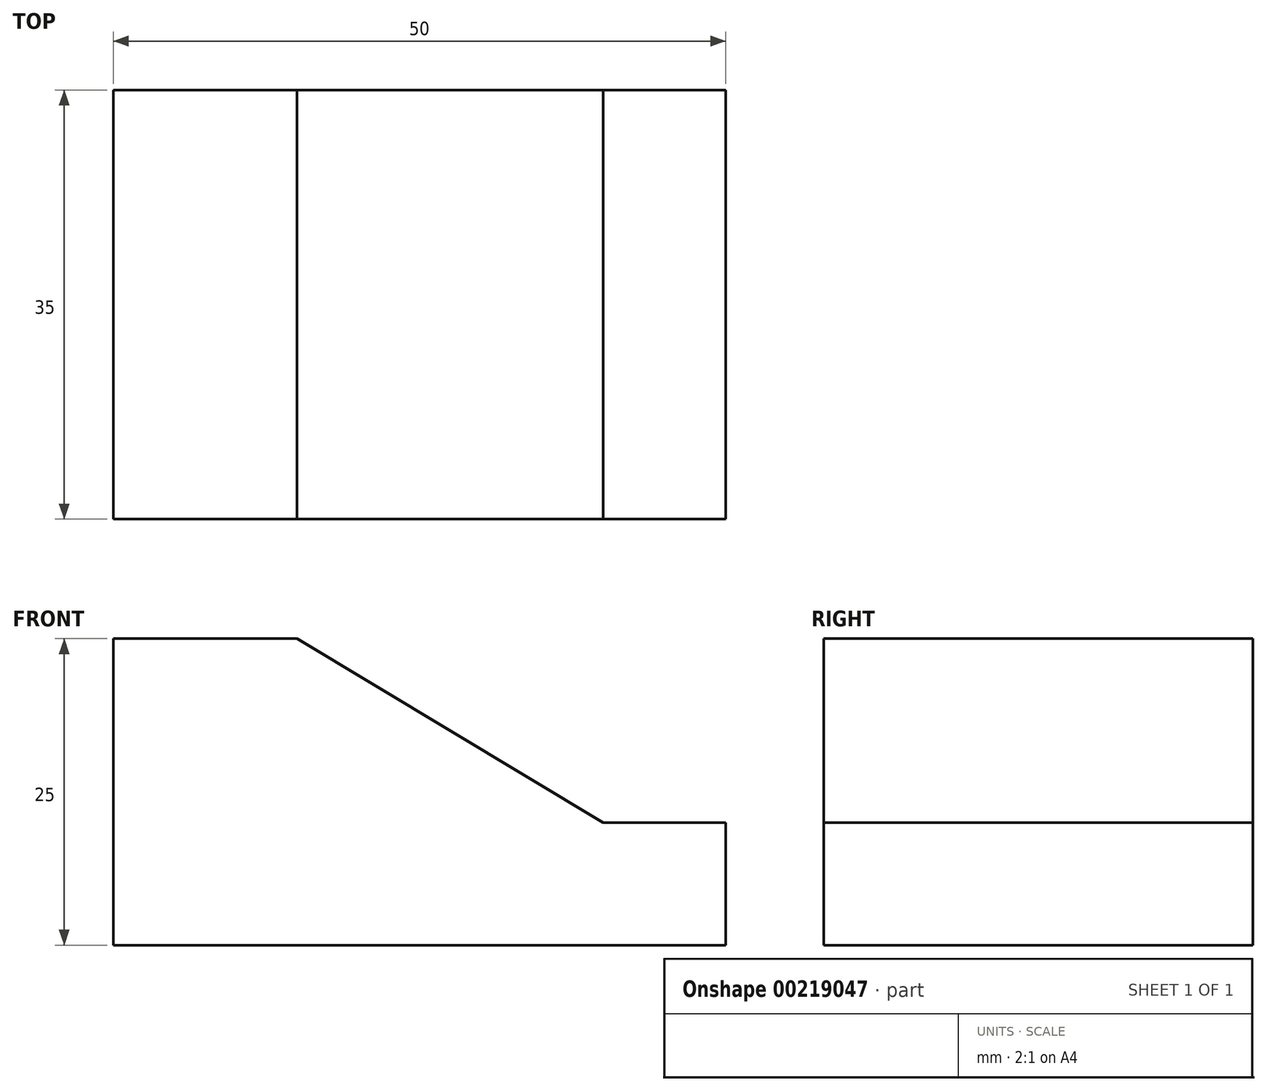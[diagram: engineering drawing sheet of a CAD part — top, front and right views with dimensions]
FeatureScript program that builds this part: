
annotation { "Feature Type Name" : "Feature", "Feature Type Description" : "" }
export const myFeature = defineFeature(function(context is Context, id is Id, definition is map)
    precondition{}
    {
        {
            var Q0;
            Q0=qCreatedBy(makeId("Front.planeOp"),FACE);
            var sketch = newSketch(context, id + "F0", { "sketchPlane" : qUnion([Q0])});
            skLineSegment(sketch, "E0", {"start": v(0, 25) * mm, "end": v(0, 0) * mm});
            skLineSegment(sketch, "E1", {"start": v(0, 0) * mm, "end": v(50, 0) * mm});
            skLineSegment(sketch, "E2", {"start": v(50, 0) * mm, "end": v(50, 10) * mm});
            skLineSegment(sketch, "E3", {"start": v(50, 10) * mm, "end": v(40, 10) * mm});
            skLineSegment(sketch, "E4", {"start": v(40, 10) * mm, "end": v(15, 25) * mm});
            skLineSegment(sketch, "E5", {"start": v(15, 25) * mm, "end": v(0, 25) * mm});
            skSolve(sketch);
        }
        {
            var Q0;
            Q0=makeQuery(id+"F0.imprint","IMPRINT",FACE,{"disambiguationData":[TD([[makeQuery(id+"F0.imprint","IMPRINT",EDGE,{"derivedFrom":sQuery(id+"F0.wireOp",EDGE,"E0")}),1.0]])]});
            extrude(context, id + "F1", {"entities" : qUnion([Q0]), "depth" : 35 * mm});
        }
    });
